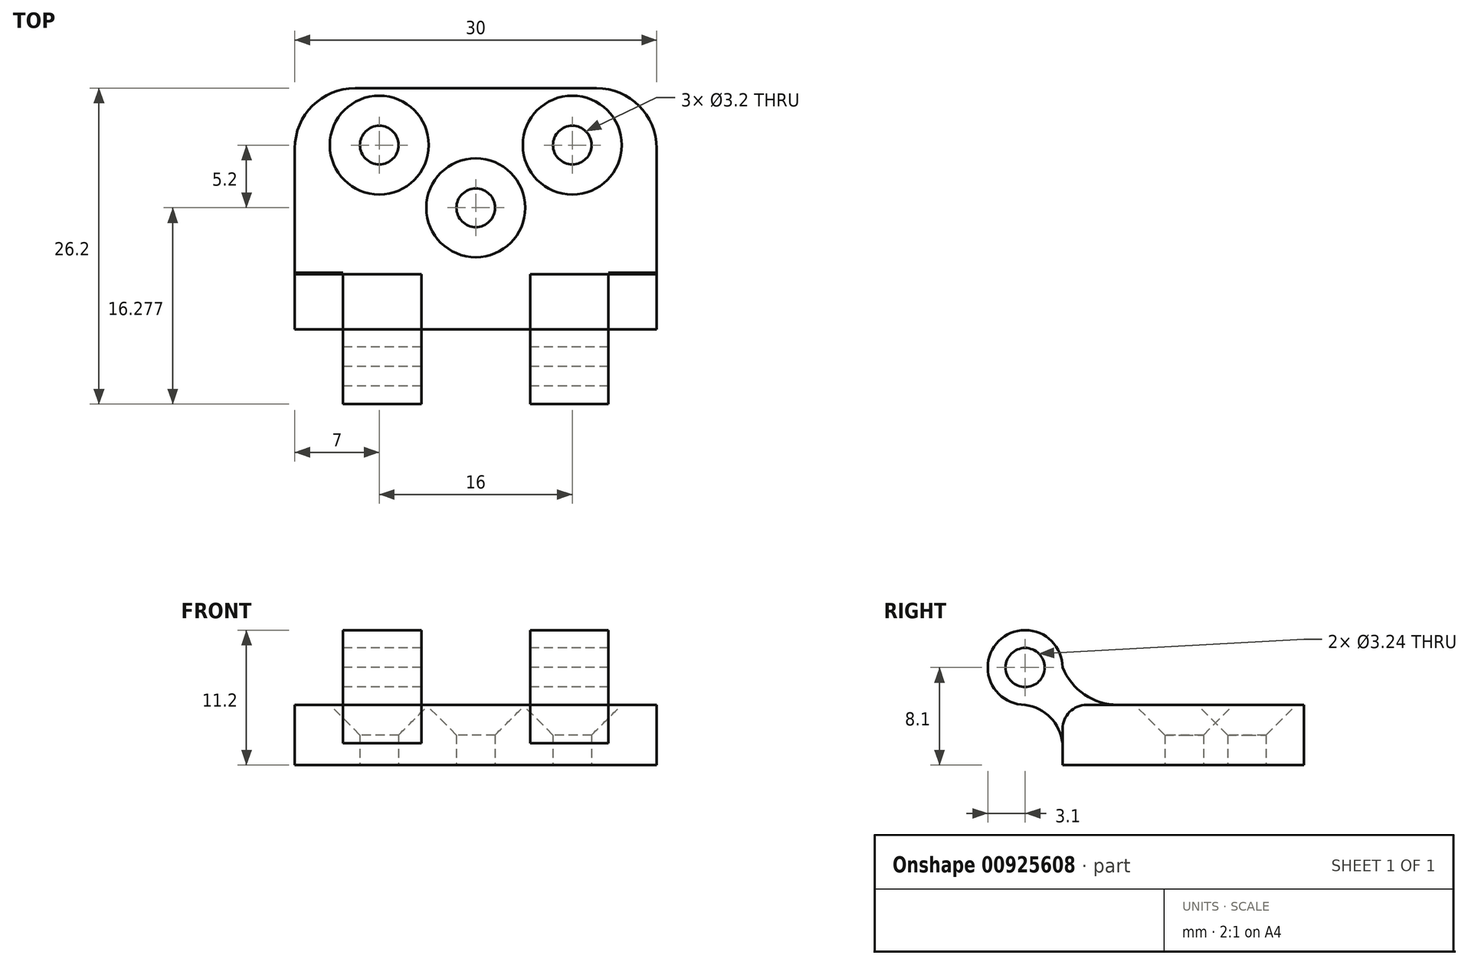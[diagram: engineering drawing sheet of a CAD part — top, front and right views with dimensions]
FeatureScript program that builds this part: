
annotation { "Feature Type Name" : "Feature", "Feature Type Description" : "" }
export const myFeature = defineFeature(function(context is Context, id is Id, definition is map)
    precondition{}
    {
        {
            var Q0;
            Q0=qCreatedBy(makeId("Top.planeOp"),FACE);
            var sketch = newSketch(context, id + "F0", { "sketchPlane" : qUnion([Q0])});
            skLineSegment(sketch, "E0.bottom", {"start": v(15, -10) * mm, "end": v(-15, -10) * mm});
            skLineSegment(sketch, "E0.top", {"start": v(15, 10) * mm, "end": v(-15, 10) * mm});
            skLineSegment(sketch, "E0.left", {"start": v(15, -10) * mm, "end": v(15, 10) * mm});
            skLineSegment(sketch, "E0.right", {"start": v(-15, -10) * mm, "end": v(-15, 10) * mm});
            skPoint(sketch, "E0.middle", {"position": v(0, 0) * mm});
            skCircle(sketch, "E1", {"center": v(-8, 5.28) * mm, "radius": 1.6 * mm});
            skCircle(sketch, "E2", {"center": v(8, 5.28) * mm, "radius": 1.6 * mm});
            skCircle(sketch, "E3", {"center": v(0, 0.08) * mm, "radius": 1.6 * mm});
            skLineSegment(sketch, "E4", {"start": v(0, 6.07) * mm, "end": v(0, -5.47) * mm, "construction": true});
            skLineSegment(sketch, "E5", {"start": v(-6.28, 0) * mm, "end": v(5.95, 0) * mm, "construction": true});
            skSolve(sketch);
        }
        {
            var Q0;
            Q0=qSketchRegion(id+"F0",true);
            extrude(context, id + "F1", {"entities" : qUnion([Q0]), "depth" : 5 * mm, "offsetDistance" : 25 * mm});
        }
        {
            var Q0;
            Q0=makeQuery(id+"F1.opExtrude","SWEPT_FACE",FACE,{"disambiguationData":[OSD([sQuery(id+"F0.wireOp",EDGE,"E0.right")])]});
            var sketch = newSketch(context, id + "F2", { "sketchPlane" : qUnion([Q0])});
            skLineSegment(sketch, "E6.bottom", {"start": v(10, 5) * mm, "end": v(16.2, 5) * mm, "construction": true});
            skLineSegment(sketch, "E6.top", {"start": v(10, 11.2) * mm, "end": v(16.2, 11.2) * mm, "construction": true});
            skLineSegment(sketch, "E6.left", {"start": v(10, 5) * mm, "end": v(10, 11.2) * mm, "construction": true});
            skLineSegment(sketch, "E6.right", {"start": v(16.2, 5) * mm, "end": v(16.2, 11.2) * mm, "construction": true});
            skCircle(sketch, "E7", {"center": v(13.1, 8.1) * mm, "radius": 3.1 * mm});
            skPoint(sketch, "E7.centerSnap0", {"position": v(16.2, 8.1) * mm});
            skPoint(sketch, "E7.centerSnap1", {"position": v(13.1, 11.2) * mm});
            skArc(sketch, "E8", {"start": v(5.31, 5) * mm, "mid": v(8.13, 5.83) * mm, "end": v(10, 8.1) * mm});
            skPoint(sketch, "E8.first.point", {"position": v(5.31, 5) * mm});
            skPoint(sketch, "E8.second.point", {"position": v(10, 8.1) * mm});
            skPoint(sketch, "E8.third.point", {"position": v(5.43, 5) * mm});
            skArc(sketch, "E9", {"start": v(13.1, 5) * mm, "mid": v(11, 3.95) * mm, "end": v(10, 1.82) * mm});
            skPoint(sketch, "E9.first.point", {"position": v(10, 1.82) * mm});
            skPoint(sketch, "E9.second.point", {"position": v(13.1, 5) * mm});
            skPoint(sketch, "E9.third.point", {"position": v(10, 1.07) * mm});
            skSolve(sketch);
        }
        {
            var Q0;
            Q0=qSketchRegion(id+"F2",true);
            var Q1;
            {var subQ0=sQuery(id+"F2.wireOp",EDGE,"E9");Q1=makeQuery(id+"F2.imprint","IMPRINT",FACE,{"disambiguationData":[TD([[makeQuery(id+"F2.imprint","IMPRINT",EDGE,{"derivedFrom":subQ0}),-1.0]])]});}
            var Q2;
            Q2=makeQuery(id+"F1.opExtrude","CAP_VERTEX",VERTEX,{"disambiguationData":[OSD([sQuery(id+"F0.wireOp",EDGE,"E0.bottom"),sQuery(id+"F0.wireOp",EDGE,"E0.left")])],"isStart":false});
            extrude(context, id + "F3", {"entities" : qUnion([Q0, Q1]), "operationType" : NewBodyOperationType.ADD, "endBound" : BoundingType.UP_TO_VERTEX, "oppositeDirection" : true, "depth" : 4 * mm, "endBoundEntityVertex" : qUnion([Q2]), "offsetDistance" : 25 * mm});
        }
        {
            var Q0;
            {var subQ0=sQuery(id+"F0.wireOp",EDGE,"E0.right");Q0=makeQuery(id+"F3.boolean.opBoolean","MERGE",FACE,{"derivedFrom":[makeQuery(id+"F1.opExtrude","SWEPT_FACE",FACE,{"disambiguationData":[OSD([subQ0])]}),makeQuery(id+"F3.opExtrude","CAP_FACE",FACE,{"disambiguationData":[OSD([sQuery(id+"F0.wireOp",EDGE,"E0.bottom"),subQ0,sQuery(id+"F2.wireOp",EDGE,"E7"),sQuery(id+"F2.wireOp",EDGE,"E8"),sQuery(id+"F2.wireOp",EDGE,"E9")])],"isStart":true})]});}
            cPlane(context, id + "F4", {"entities" : qUnion([Q0]), "cplaneType" : CPlaneType.OFFSET, "offset" : 4 * mm, "oppositeDirection" : true, "width" : 150 * mm, "height" : 150 * mm});
        }
        {
            var Q0;
            Q0=makeQuery(id+"F3.boolean.opBoolean","MERGE",FACE,{"derivedFrom":[makeQuery(id+"F1.opExtrude","SWEPT_FACE",FACE,{"disambiguationData":[OSD([sQuery(id+"F0.wireOp",EDGE,"E0.left")])]}),makeQuery(id+"F3.opExtrude","CAP_FACE",FACE,{"disambiguationData":[OSD([sQuery(id+"F0.wireOp",EDGE,"E0.bottom"),sQuery(id+"F0.wireOp",EDGE,"E0.right"),sQuery(id+"F2.wireOp",EDGE,"E7"),sQuery(id+"F2.wireOp",EDGE,"E8"),sQuery(id+"F2.wireOp",EDGE,"E9")])],"isStart":false})]});
            cPlane(context, id + "F5", {"entities" : qUnion([Q0]), "cplaneType" : CPlaneType.OFFSET, "offset" : 4 * mm, "oppositeDirection" : true, "width" : 150 * mm, "height" : 150 * mm});
        }
        {
            var Q0;
            Q0=qCreatedBy(id+"F5.planeOp",FACE);
            var sketch = newSketch(context, id + "F6", { "sketchPlane" : qUnion([Q0])});
            skPoint(sketch, "E10.MirrorP", {"position": v(-5.43, 5) * mm});
            skLineSegment(sketch, "E11.MirrorCS", {"start": v(-10, 5) * mm, "end": v(-16.2, 5) * mm, "construction": true});
            skCircle(sketch, "E12.MirrorC", {"center": v(-13.1, 8.1) * mm, "radius": 3.1 * mm});
            skPoint(sketch, "E13.MirrorP", {"position": v(-10, 8.1) * mm});
            skArc(sketch, "E14.MirrorCS", {"start": v(-13.1, 5) * mm, "mid": v(-11, 3.95) * mm, "end": v(-10, 1.82) * mm});
            skPoint(sketch, "E15.MirrorP", {"position": v(-5.31, 5) * mm});
            skArc(sketch, "E16.MirrorCS", {"start": v(-5.31, 5) * mm, "mid": v(-8.13, 5.83) * mm, "end": v(-10, 8.1) * mm});
            skPoint(sketch, "E17.MirrorP", {"position": v(-10, 1.82) * mm});
            skLineSegment(sketch, "E18.MirrorCS", {"start": v(-16.2, 5) * mm, "end": v(-16.2, 11.2) * mm, "construction": true});
            skPoint(sketch, "E19.MirrorP", {"position": v(-13.1, 5) * mm});
            skPoint(sketch, "E20.MirrorP", {"position": v(-13.1, 11.2) * mm});
            skLineSegment(sketch, "E21.MirrorCS", {"start": v(-10, 5) * mm, "end": v(-10, 11.2) * mm, "construction": true});
            skPoint(sketch, "E22.MirrorP", {"position": v(-16.2, 8.1) * mm});
            skLineSegment(sketch, "E23.MirrorCS", {"start": v(-10, 11.2) * mm, "end": v(-16.2, 11.2) * mm, "construction": true});
            skArc(sketch, "E24.0", {"start": v(-13.1, 5) * mm, "mid": v(-11, 3.95) * mm, "end": v(-10, 1.82) * mm, "construction": true});
            skLineSegment(sketch, "E25", {"start": v(-10, 1.82) * mm, "end": v(-10, 5) * mm});
            skLineSegment(sketch, "E26", {"start": v(-10, 5) * mm, "end": v(-5.31, 5) * mm});
            skSolve(sketch);
        }
        {
            var Q0;
            Q0=qSketchRegion(id+"F6",true);
            extrude(context, id + "F7", {"entities" : qUnion([Q0]), "operationType" : NewBodyOperationType.REMOVE, "depth" : 7 * mm, "offsetDistance" : 25 * mm});
        }
        {
            var Q0;
            Q0=qCreatedBy(id+"F4.planeOp",FACE);
            var sketch = newSketch(context, id + "F8", { "sketchPlane" : qUnion([Q0])});
            skLineSegment(sketch, "E27.bottom", {"start": v(10, 5) * mm, "end": v(16.2, 5) * mm, "construction": true});
            skLineSegment(sketch, "E27.top", {"start": v(10, 11.2) * mm, "end": v(16.2, 11.2) * mm, "construction": true});
            skLineSegment(sketch, "E27.left", {"start": v(10, 5) * mm, "end": v(10, 11.2) * mm, "construction": true});
            skLineSegment(sketch, "E27.right", {"start": v(16.2, 5) * mm, "end": v(16.2, 11.2) * mm, "construction": true});
            skCircle(sketch, "E28", {"center": v(13.1, 8.1) * mm, "radius": 3.1 * mm});
            skPoint(sketch, "E28.centerSnap0", {"position": v(16.2, 8.1) * mm});
            skPoint(sketch, "E28.centerSnap1", {"position": v(13.1, 11.2) * mm});
            skArc(sketch, "E29", {"start": v(5.31, 5) * mm, "mid": v(8.13, 5.83) * mm, "end": v(10, 8.1) * mm});
            skPoint(sketch, "E29.first.point", {"position": v(5.31, 5) * mm});
            skPoint(sketch, "E29.second.point", {"position": v(10, 8.1) * mm});
            skPoint(sketch, "E29.third.point", {"position": v(5.43, 5) * mm});
            skArc(sketch, "E30", {"start": v(13.1, 5) * mm, "mid": v(11, 3.95) * mm, "end": v(10, 1.82) * mm});
            skPoint(sketch, "E30.first.point", {"position": v(10, 1.82) * mm});
            skPoint(sketch, "E30.second.point", {"position": v(13.1, 5) * mm});
            skArc(sketch, "E31.0", {"start": v(13.1, 5) * mm, "mid": v(11, 3.95) * mm, "end": v(10, 1.82) * mm, "construction": true});
            skLineSegment(sketch, "E32", {"start": v(10, 1.82) * mm, "end": v(10, 5) * mm});
            skLineSegment(sketch, "E33", {"start": v(10, 5) * mm, "end": v(5.31, 5) * mm});
            skSolve(sketch);
        }
        {
            var Q0;
            Q0=qSketchRegion(id+"F8",true);
            extrude(context, id + "F9", {"entities" : qUnion([Q0]), "operationType" : NewBodyOperationType.REMOVE, "depth" : 7 * mm, "offsetDistance" : 25 * mm});
        }
        {
            var Q0;
            Q0=makeQuery(id+"F1.opExtrude","CAP_EDGE",EDGE,{"disambiguationData":[OSD([sQuery(id+"F0.wireOp",EDGE,"E1")])],"isStart":false});
            var Q1;
            Q1=makeQuery(id+"F1.opExtrude","CAP_EDGE",EDGE,{"disambiguationData":[OSD([sQuery(id+"F0.wireOp",EDGE,"E3")])],"isStart":false});
            var Q2;
            Q2=makeQuery(id+"F1.opExtrude","CAP_EDGE",EDGE,{"disambiguationData":[OSD([sQuery(id+"F0.wireOp",EDGE,"E2")])],"isStart":false});
            chamfer(context, id + "F10", {"entities" : qUnion([Q0, Q1, Q2]), "width" : 2.5 * mm, "tangentPropagation" : true});
        }
        {
            var Q0;
            Q0=makeQuery(id+"F1.opExtrude","SWEPT_EDGE",EDGE,{"disambiguationData":[OSD([sQuery(id+"F0.wireOp",EDGE,"E0.top"),sQuery(id+"F0.wireOp",EDGE,"E0.right")])]});
            var Q1;
            Q1=makeQuery(id+"F1.opExtrude","SWEPT_EDGE",EDGE,{"disambiguationData":[OSD([sQuery(id+"F0.wireOp",EDGE,"E0.top"),sQuery(id+"F0.wireOp",EDGE,"E0.left")])]});
            fillet(context, id + "F11", {"entities" : qUnion([Q0, Q1]), "radius" : 5 * mm, "tangentPropagation" : true, "allowEdgeOverflow" : false});
        }
        {
            var Q0;
            {var subQ0=sQuery(id+"F0.wireOp",EDGE,"E0.right");Q0=makeQuery(id+"F3.boolean.opBoolean","MERGE",FACE,{"derivedFrom":[makeQuery(id+"F1.opExtrude","SWEPT_FACE",FACE,{"disambiguationData":[OSD([subQ0])]}),makeQuery(id+"F3.opExtrude","CAP_FACE",FACE,{"disambiguationData":[OSD([sQuery(id+"F0.wireOp",EDGE,"E0.bottom"),subQ0,sQuery(id+"F2.wireOp",EDGE,"E7"),sQuery(id+"F2.wireOp",EDGE,"E8"),sQuery(id+"F2.wireOp",EDGE,"E9")])],"isStart":true})]});}
            var sketch = newSketch(context, id + "F12", { "sketchPlane" : qUnion([Q0])});
            skArc(sketch, "E34.0", {"start": v(13.1, 5) * mm, "mid": v(15.3, 10.3) * mm, "end": v(10, 8.1) * mm, "construction": true});
            skCircle(sketch, "E35", {"center": v(13.1, 8.1) * mm, "radius": 1.62 * mm});
            skSolve(sketch);
        }
        {
            var Q0;
            Q0=makeQuery(id+"F12.imprint","IMPRINT",FACE,{"disambiguationData":[TD([[makeQuery(id+"F12.imprint","IMPRINT",EDGE,{"derivedFrom":sQuery(id+"F12.wireOp",EDGE,"E35")}),1.0]])]});
            extrude(context, id + "F13", {"entities" : qUnion([Q0]), "operationType" : NewBodyOperationType.REMOVE, "endBound" : BoundingType.THROUGH_ALL, "oppositeDirection" : true, "depth" : 25 * mm, "offsetDistance" : 25 * mm});
        }
        {
            var Q0;
            Q0=makeQuery(id+"F9.boolean.opBoolean","COPY",EDGE,{"derivedFrom":makeQuery(id+"F9.opExtrude","SWEPT_EDGE",EDGE,{"disambiguationData":[OSD([sQuery(id+"F8.wireOp",EDGE,"E32"),sQuery(id+"F8.wireOp",EDGE,"E33")])]})});
            var Q1;
            Q1=makeQuery(id+"F7.boolean.opBoolean","COPY",EDGE,{"derivedFrom":makeQuery(id+"F7.opExtrude","SWEPT_EDGE",EDGE,{"disambiguationData":[OSD([sQuery(id+"F6.wireOp",EDGE,"E25"),sQuery(id+"F6.wireOp",EDGE,"E26")])]})});
            fillet(context, id + "F14", {"entities" : qUnion([Q0, Q1]), "radius" : 2 * mm, "tangentPropagation" : true, "allowEdgeOverflow" : false});
        }
        {
            var Q0;
            Q0=makeQuery(id+"F9.boolean.opBoolean","COPY",FACE,{"derivedFrom":makeQuery(id+"F9.opExtrude","CAP_FACE",FACE,{"disambiguationData":[OSD([sQuery(id+"F8.wireOp",EDGE,"E28"),sQuery(id+"F8.wireOp",EDGE,"E29"),sQuery(id+"F8.wireOp",EDGE,"E30"),sQuery(id+"F8.wireOp",EDGE,"E32"),sQuery(id+"F8.wireOp",EDGE,"E33")])],"isStart":true})});
            cPlane(context, id + "F15", {"entities" : qUnion([Q0]), "cplaneType" : CPlaneType.OFFSET, "offset" : 6.5 * mm, "oppositeDirection" : true, "width" : 150 * mm, "height" : 150 * mm});
        }
        {
            var Q0;
            Q0=qCreatedBy(id+"F15.planeOp",FACE);
            var sketch = newSketch(context, id + "F16", { "sketchPlane" : qUnion([Q0])});
            skArc(sketch, "E36.0.0", {"start": v(13.1, 5) * mm, "mid": v(15.3, 10.3) * mm, "end": v(10, 8.1) * mm});
            skArc(sketch, "E36.0.1", {"start": v(10, 8.1) * mm, "mid": v(8.18, 5.86) * mm, "end": v(5.43, 5) * mm});
            skLineSegment(sketch, "E36.0.2", {"start": v(5.43, 5) * mm, "end": v(8, 5) * mm});
            skArc(sketch, "E36.0.3", {"start": v(8, 5) * mm, "mid": v(9.41, 4.41) * mm, "end": v(10, 3) * mm});
            skLineSegment(sketch, "E36.0.4", {"start": v(10, 3) * mm, "end": v(10, 1.82) * mm});
            skArc(sketch, "E36.0.5", {"start": v(10, 1.82) * mm, "mid": v(11, 3.95) * mm, "end": v(13.1, 5) * mm});
            skSolve(sketch);
        }
        {
            var Q0;
            Q0 = qSketchRegion(id + "F16", true);
            extrude(context, id + "F17", {"entities" : qUnion([Q0]), "operationType" : NewBodyOperationType.REMOVE, "oppositeDirection" : true, "depth" : 9 * mm, "offsetDistance" : 25 * mm});
        }
    });
